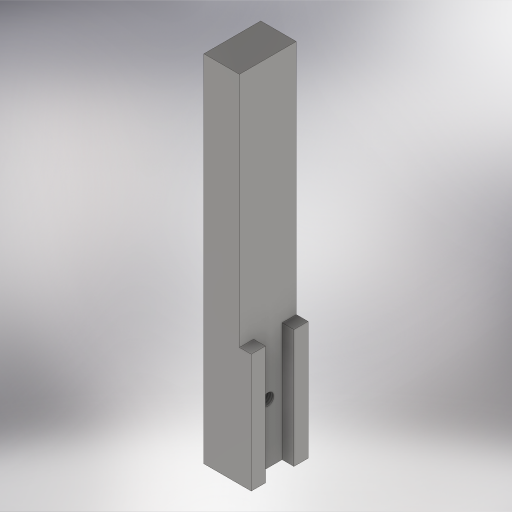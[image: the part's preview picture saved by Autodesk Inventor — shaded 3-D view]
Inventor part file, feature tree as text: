
AUTODESK INVENTOR PART (.ipt)
format: ipt  version: 2023 (Build 270158000, 158)  size: 667,648 bytes
history: native  units: mm
features: sketch x3, extrude x2, other x1, hole x1
ambient origin geometry x8: Origin, YZ Plane, XZ Plane, XY Plane, X Axis, Y Axis, Z Axis, Center Point
bodies: Body1 (feature_tree)
feature tree (7):
  other  "Sólido1"
  extrude  "Extrusão1"  Depth=24.0mm
  extrude  "Extrusão2"  Depth=12.0mm
  hole  "Furo1"  [1 undecoded]
  sketch  "Esboço1"  dims[d0=15.0mm d1=24.0mm]
  sketch  "Esboço2"  dims[d2=149.8mm d3=0.0mm d4=12.0mm]
  sketch  "Esboço3"  dims[d5=50.0mm d6=5.0mm d7=0.0mm d8=25.0mm d9=24.0mm d10=12.0mm d11=4.917mm d12=12.0mm d13=4.0mm d14=2.0mm d15=90.0deg d16=0.5mm d17=20.594885mm]
note: 1 required parameter value undecoded (feature->parameter linkage not recoverable at this tier; creation-order binding heuristic only, values carry confidence <= 0.55)
